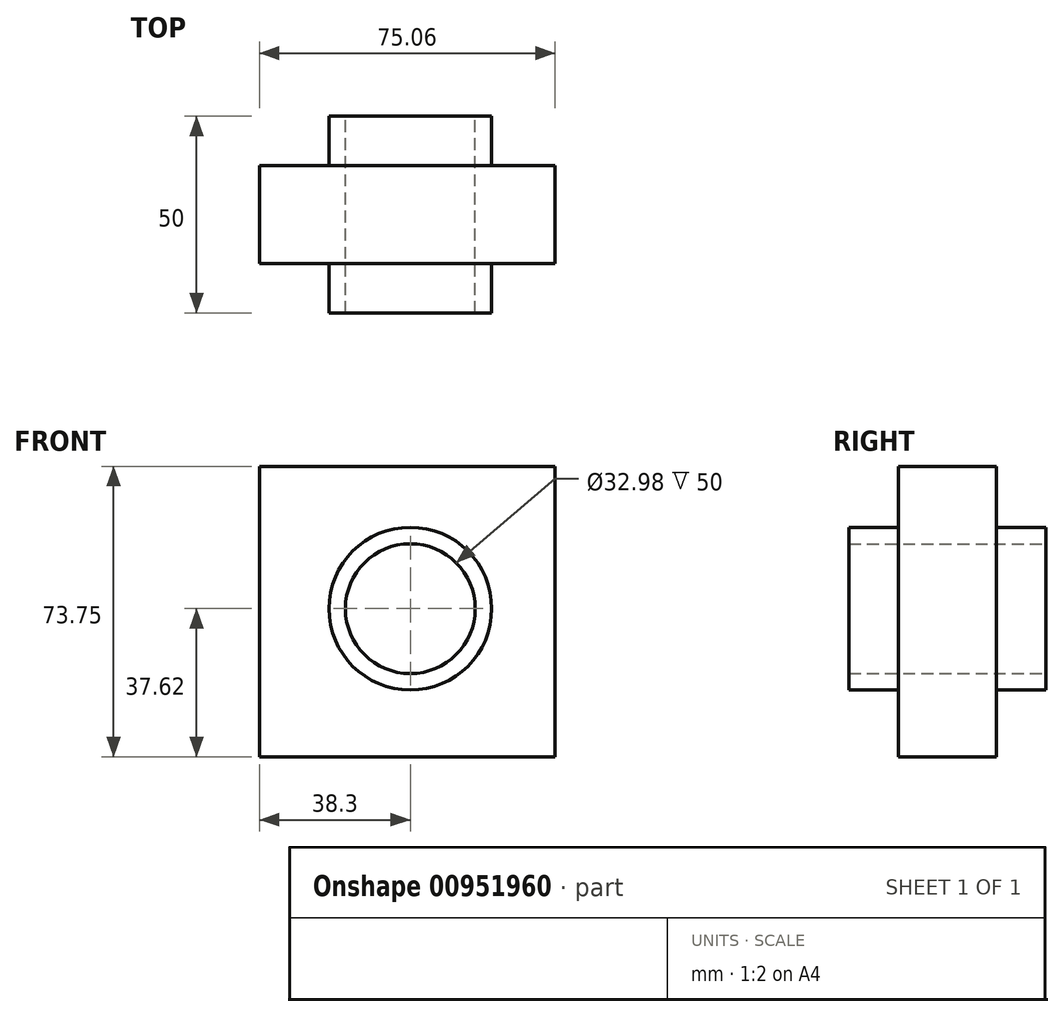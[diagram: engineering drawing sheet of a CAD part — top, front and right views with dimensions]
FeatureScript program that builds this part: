
annotation { "Feature Type Name" : "Feature", "Feature Type Description" : "" }
export const myFeature = defineFeature(function(context is Context, id is Id, definition is map)
    precondition{}
    {
        {
            var Q0;
            Q0=qCreatedBy(makeId("Front.planeOp"),FACE);
            var sketch = newSketch(context, id + "F0", { "sketchPlane" : qUnion([Q0])});
            skLineSegment(sketch, "E0.bottom", {"start": v(-38.3, 36.13) * mm, "end": v(36.76, 36.13) * mm});
            skLineSegment(sketch, "E0.top", {"start": v(-38.3, -37.62) * mm, "end": v(36.76, -37.62) * mm});
            skLineSegment(sketch, "E0.left", {"start": v(-38.3, 36.13) * mm, "end": v(-38.3, -37.62) * mm});
            skLineSegment(sketch, "E0.right", {"start": v(36.76, 36.13) * mm, "end": v(36.76, -37.62) * mm});
            skCircle(sketch, "E1", {"center": v(0, 0) * mm, "radius": 16.2 * mm});
            skCircle(sketch, "E2", {"center": v(0, 0) * mm, "radius": 20.56 * mm});
            skSolve(sketch);
        }
        {
            var Q0;
            Q0 = qSketchRegion(id + "F0", true);
            extrude(context, id + "F1", {"entities" : qUnion([Q0]), "depth" : 25 * mm, "offsetDistance" : 25 * mm, "symmetric" : true});
        }
        {
            var Q0;
            Q0=qCreatedBy(makeId("Front.planeOp"),FACE);
            var sketch = newSketch(context, id + "F2", { "sketchPlane" : qUnion([Q0])});
            skCircle(sketch, "E3", {"center": v(0, 0) * mm, "radius": 20.67 * mm});
            skCircle(sketch, "E4", {"center": v(0, 0) * mm, "radius": 16.49 * mm});
            skSolve(sketch);
        }
        {
            var Q0;
            Q0=makeQuery(id+"F2.imprint","IMPRINT",FACE,{"disambiguationData":[TD([[makeQuery(id+"F2.imprint","IMPRINT",EDGE,{"derivedFrom":sQuery(id+"F2.wireOp",EDGE,"E3")}),1.0]])]});
            extrude(context, id + "F3", {"entities" : qUnion([Q0]), "operationType" : NewBodyOperationType.ADD, "depth" : 50 * mm, "offsetDistance" : 25 * mm, "symmetric" : true});
        }
    });
